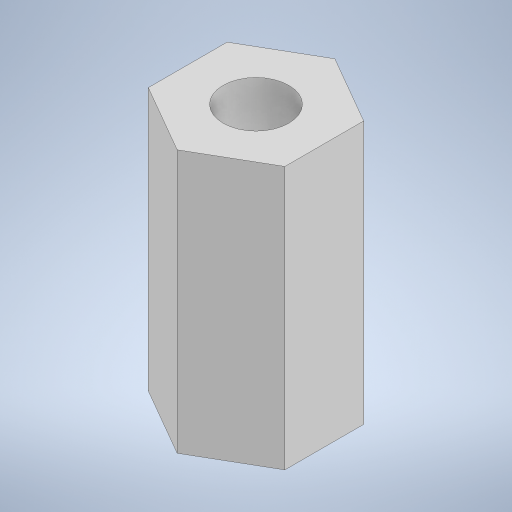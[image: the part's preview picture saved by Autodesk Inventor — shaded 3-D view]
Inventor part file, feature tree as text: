
AUTODESK INVENTOR PART (.ipt)
format: ipt  version: 2023 (Build 270158000, 158)  size: 222,208 bytes
history: native  units: in
note: dims shown in document units (in); Inventor stores cm internally (conversion verified against a paired STEP export)
features: extrude x1, sketch x1
ambient origin geometry x8: Origin, YZ Plane, XZ Plane, XY Plane, X Axis, Y Axis, Z Axis, Center Point
bodies: Solid1 (feature_tree)
feature tree (2):
  extrude  "Extrusion1"  Depth=0.3937in TaperAngle=0.0deg
  sketch  "Sketch1"  dims[d0=0.0984in d2=0.3937in d3=0.0in]
